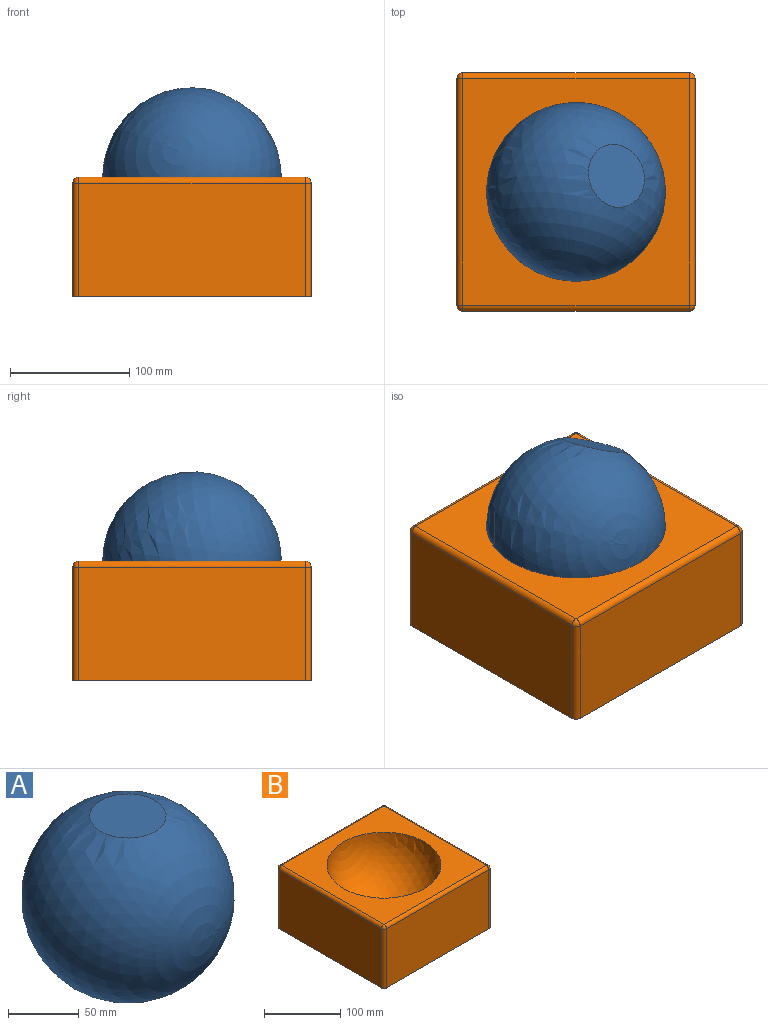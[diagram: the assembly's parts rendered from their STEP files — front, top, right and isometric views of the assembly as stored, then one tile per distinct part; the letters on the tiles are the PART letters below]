
ASSEMBLY  parts=2 mates=1
PART A: 2 faces, bbox 150x150x150 mm
  f0: sphere r=75mm, area 68329.5mm2, adj f1
  f1: plane 53.85x53.85mm, normal (0,0,1), area 2277.7mm2, adj f0
PART B: 41 faces, bbox 200x200x114.6 mm
  f0: plane 190x95mm, normal (1,0,0), area 18050mm2, adj f4,f9,f15,f18
  f1: plane 190x95mm, normal (0,1,0), area 18050mm2, adj f4,f12,f16,f18
  f2: plane 190x95mm, normal (-1,0,0), area 18050mm2, adj f4,f7,f11,f12
  f3: plane 190x95mm, normal (0,-1,0), area 18050mm2, adj f4,f7,f9,f10
  f4: plane 200x200mm, normal (0,0,-1), area 3684.2mm2, adj f0,f1,f2,f3,f7,f9,f12,f18
  f5: plane 190x190mm, normal (0,0,1), area 18405mm2, adj f6,f10,f11,f15,f16
  f6: sphere r=75.05mm, area 35390.1mm2, adj f5
  f7: cylinder r=5mm len=95mm, axis (0,0,-1), area 746.1mm2, adj f2,f3,f4,f8
  f8: sphere r=5mm, area 39.3mm2, adj f7,f10,f11
  f9: cylinder r=5mm len=95mm, axis (0,0,1), area 746.1mm2, adj f0,f3,f4,f13
  f10: cylinder r=5mm len=190mm, axis (1,0,0), area 1492.3mm2, adj f3,f5,f8,f13
  f11: cylinder r=5mm len=190mm, axis (0,-1,0), area 1492.3mm2, adj f2,f5,f8,f14
  f12: cylinder r=5mm len=95mm, axis (0,0,1), area 746.1mm2, adj f1,f2,f4,f14
  f13: sphere r=5mm, area 39.3mm2, adj f9,f10,f15
  f14: sphere r=5mm, area 39.3mm2, adj f11,f12,f16
  f15: cylinder r=5mm len=190mm, axis (0,1,0), area 1492.3mm2, adj f0,f5,f13,f17
  f16: cylinder r=5mm len=190mm, axis (-1,0,0), area 1492.3mm2, adj f1,f5,f14,f17
  f17: sphere r=5mm, area 39.3mm2, adj f15,f16,f18
  f18: cylinder r=5mm len=95mm, axis (0,0,-1), area 746.1mm2, adj f0,f1,f4,f17
  f19: plane 188x94mm, normal (-1,0,0), area 17671.4mm2, adj f4,f30,f33,f36,f39
  f20: plane 188x93mm, normal (0,-1,0), area 17484mm2, adj f26,f27,f33,f34
  f21: plane 188x94mm, normal (1,0,0), area 17671.4mm2, adj f4,f25,f27,f28,f29
  f22: plane 188x94mm, normal (0,1,0), area 17672mm2, adj f4,f29,f35,f36
  f23: plane 188x188mm, normal (0,0,-1), area 14819.7mm2, adj f28,f34,f35,f39,f40
  f24: sphere r=80.05mm, area 37293.4mm2, adj f40
  f25: torus R=2mm, axis (0,0,1), area 4.8mm2, adj f4,f21,f26,f27
  f26: cylinder r=1mm len=188mm, axis (-1,0,0), area 295.3mm2, adj f4,f20,f25,f30
  f27: cylinder r=1mm len=93mm, axis (0,0,1), area 146.1mm2, adj f20,f21,f25,f31
  f28: cylinder r=1mm len=188mm, axis (0,1,0), area 295.3mm2, adj f21,f23,f31,f32
  f29: cylinder r=1mm len=94mm, axis (0,0,1), area 147.7mm2, adj f4,f21,f22,f32
  f30: torus R=2mm, axis (0,0,1), area 4.8mm2, adj f4,f19,f26,f33
  f31: sphere r=1mm, area 1.6mm2, adj f27,f28,f34
  f32: sphere r=1mm, area 1.6mm2, adj f28,f29,f35
  f33: cylinder r=1mm len=93mm, axis (0,0,-1), area 146.1mm2, adj f19,f20,f30,f37
  f34: cylinder r=1mm len=188mm, axis (1,0,0), area 295.3mm2, adj f20,f23,f31,f37
  f35: cylinder r=1mm len=188mm, axis (-1,0,0), area 295.3mm2, adj f22,f23,f32,f38
  f36: cylinder r=1mm len=94mm, axis (0,0,1), area 147.7mm2, adj f4,f19,f22,f38
  f37: sphere r=1mm, area 1.6mm2, adj f33,f34,f39
  f38: sphere r=1mm, area 1.6mm2, adj f35,f36,f39
  f39: cylinder r=1mm len=188mm, axis (0,-1,0), area 295.3mm2, adj f19,f23,f37,f38
  f40: torus R=80.83mm, axis (0,0,1), area 754.3mm2, adj f23,f24
PLACE A rot(axis=(0.24,0.13,0.96),166.6deg) t=(0,0,0)mm
PLACE B at identity fixed
MATE ball A.f0 <-> B.f40  axis (0.48,0.19,0.85) through (0,0,0)mm
